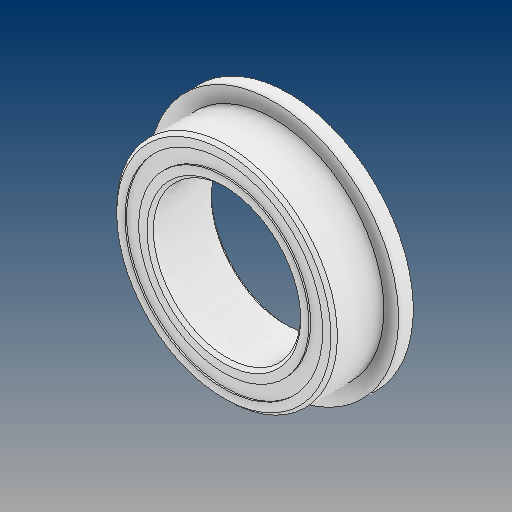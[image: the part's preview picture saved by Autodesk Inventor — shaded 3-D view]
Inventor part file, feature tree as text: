
AUTODESK INVENTOR PART (.ipt)
format: ipt  version: 2024.3 (Build 283343000, 343)  size: 598,528 bytes
history: native  units: in
note: dims shown in document units (in); Inventor stores cm internally (conversion verified against a paired STEP export)
features: other x11, revolve x5
ambient origin geometry x8: Origin, YZ Plane, XZ Plane, XY Plane, X Axis, Y Axis, Z Axis, Center Point
bodies: Solid1 (feature_tree), Solid2 (feature_tree), Solid3 (feature_tree), Solid4 (feature_tree), Solid5 (feature_tree), Solid6 (feature_tree), Solid7 (feature_tree), Solid8 (feature_tree), Solid9 (feature_tree), Solid10 (feature_tree), Solid11 (feature_tree), Solid12 (feature_tree), Solid13 (feature_tree), Solid14 (feature_tree), Solid15 (feature_tree), Solid16 (feature_tree)
feature tree (16):
  revolve  "Revolve3"  [1 undecoded]
  revolve  "Revolve4"  [1 undecoded]
  other  "CirPattern1[1]"
  other  "CirPattern1[2]"
  other  "CirPattern1[3]"
  other  "CirPattern1[4]"
  other  "CirPattern1[5]"
  other  "CirPattern1[6]"
  other  "CirPattern1[7]"
  other  "CirPattern1[8]"
  other  "CirPattern1[9]"
  other  "CirPattern1[10]"
  other  "CirPattern1[11]"
  revolve  "Revolve5[1]"  [1 undecoded]
  revolve  "Revolve5[2]"  [1 undecoded]
  revolve  "Revolve6"  [1 undecoded]
note: 5 required parameter values undecoded (feature->parameter linkage not recoverable at this tier; creation-order binding heuristic only, values carry confidence <= 0.55)
